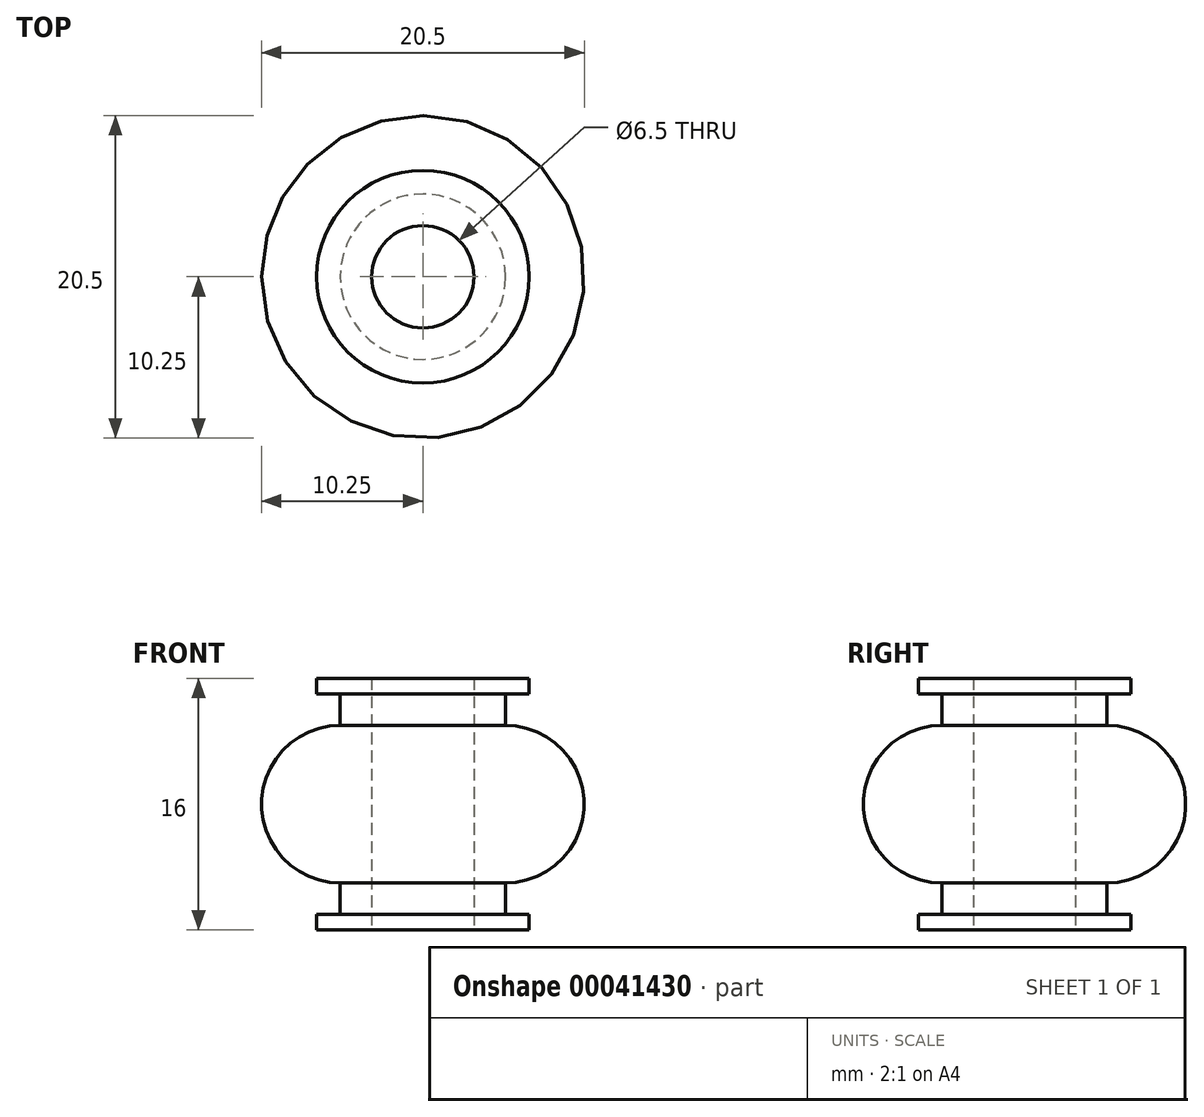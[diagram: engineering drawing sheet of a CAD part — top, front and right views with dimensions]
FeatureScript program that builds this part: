
annotation { "Feature Type Name" : "Feature", "Feature Type Description" : "" }
export const myFeature = defineFeature(function(context is Context, id is Id, definition is map)
    precondition{}
    {
        {
            var Q0;
            Q0=qCreatedBy(makeId("Front.planeOp"),FACE);
            var sketch = newSketch(context, id + "F0", { "sketchPlane" : qUnion([Q0])});
            skLineSegment(sketch, "E0", {"start": v(0, 0) * mm, "end": v(0, 30.7) * mm, "construction": true});
            skLineSegment(sketch, "E1.0", {"start": v(3.25, 0) * mm, "end": v(3.25, 16) * mm});
            skLineSegment(sketch, "E2", {"start": v(3.25, 0) * mm, "end": v(6.75, 0) * mm});
            skLineSegment(sketch, "E3", {"start": v(6.75, 0) * mm, "end": v(6.75, 1) * mm});
            skLineSegment(sketch, "E4", {"start": v(6.75, 1) * mm, "end": v(5.25, 1) * mm});
            skLineSegment(sketch, "E5.0", {"start": v(6.75, 3) * mm, "end": v(3.25, 3) * mm, "construction": true});
            skLineSegment(sketch, "E6.0", {"start": v(6.75, 13) * mm, "end": v(3.25, 13) * mm, "construction": true});
            skLineSegment(sketch, "E7.0", {"start": v(5.25, 1) * mm, "end": v(5.25, 3) * mm});
            skLineSegment(sketch, "E8.0", {"start": v(6.75, 8) * mm, "end": v(3.25, 8) * mm, "construction": true});
            skArc(sketch, "E9", {"start": v(5.25, 3) * mm, "mid": v(10.24, 8.13) * mm, "end": v(5, 13) * mm});
            skLineSegment(sketch, "E10.MirrorCS", {"start": v(6.75, 16) * mm, "end": v(6.75, 15) * mm});
            skLineSegment(sketch, "E11.MirrorCS", {"start": v(6.75, 15) * mm, "end": v(5.25, 15) * mm});
            skLineSegment(sketch, "E12.MirrorCS", {"start": v(3.25, 16) * mm, "end": v(6.75, 16) * mm});
            skLineSegment(sketch, "E13.trimOffspring", {"start": v(5.25, 13) * mm, "end": v(5.25, 15) * mm});
            skSolve(sketch);
        }
        {
            var Q0;
            Q0=makeQuery(id+"F0.imprint","IMPRINT",FACE,{"disambiguationData":[TD([[makeQuery(id+"F0.imprint","IMPRINT",EDGE,{"derivedFrom":sQuery(id+"F0.wireOp",EDGE,"E1.0")}),-1.0]])]});
            var Q1;
            Q1=sQuery(id+"F0.wireOp",EDGE,"E0");
            revolve(context, id + "F1", {"entities" : qUnion([Q0]), "axis" : qUnion([Q1]), "revolveType" : RevolveType.FULL});
        }
    });
